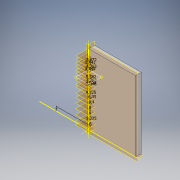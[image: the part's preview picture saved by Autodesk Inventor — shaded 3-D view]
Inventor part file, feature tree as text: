
AUTODESK INVENTOR PART (.ipt)
format: ipt  version: 2018 (Build 220112000, 112)  size: 127,488 bytes
history: native  units: in
note: dims shown in document units (in); Inventor stores cm internally (conversion verified against a paired STEP export)
features: other x25, extrude x1, sketch x1
ambient origin geometry x8: Origin, YZ Plane, XZ Plane, XY Plane, X Axis, Y Axis, Z Axis, Center Point
bodies: Solid1 (feature_tree)
feature tree (27):
  extrude  "Extrusion1"  Depth=3.1496in
  other  "Waste_Output_y"
  other  "lower_vial_2_vial_y"
  other  "mux_valves_4"
  other  "y_coordinates"
  other  "y_waste_output"
  other  "y_lower_vial_2_vial"
  other  "y_lower_mux"
  other  "y_mux_valves_1"
  other  "y_mux_valves_2"
  other  "y_mux_valves_3"
  other  "y_mux_valves_4"
  other  "y_from_vial"
  other  "y_from_vial_valves"
  other  "y_from_vial_line"
  other  "y_bypass_valves"
  other  "y_to_vial_line"
  other  "y_to_vial_valves"
  other  "y_to_vial"
  other  "y_demux_valves_1"
  other  "y_demux_valves_2"
  other  "y_demux_valves_3"
  sketch  "Sketch1"  dims[d0=4.7244in d1=3.1496in d2=0.3937in d3=0.0in d4=0.3937in d5=0.1969in d6=0.3937in d7=0.3937in d8=0.3937in d9=0.3937in d10=0.3937in d11=0.2756in d12=0.2362in d13=0.3632in d14=0.3543in d15=0.315in d16=0.3307in d17=0.25in d18=0.375in d19=0.1606in d20=0.2144in d21=0.1875in d22=0.2198in d23=0.177in d24=0.2282in d25=0.1875in d26=0.2142in d27=0.2233in]
  other  "lower_mux_y"
  other  "mux_valves_1"
  other  "mux_valves_2"
  other  "mux_valves_3"
